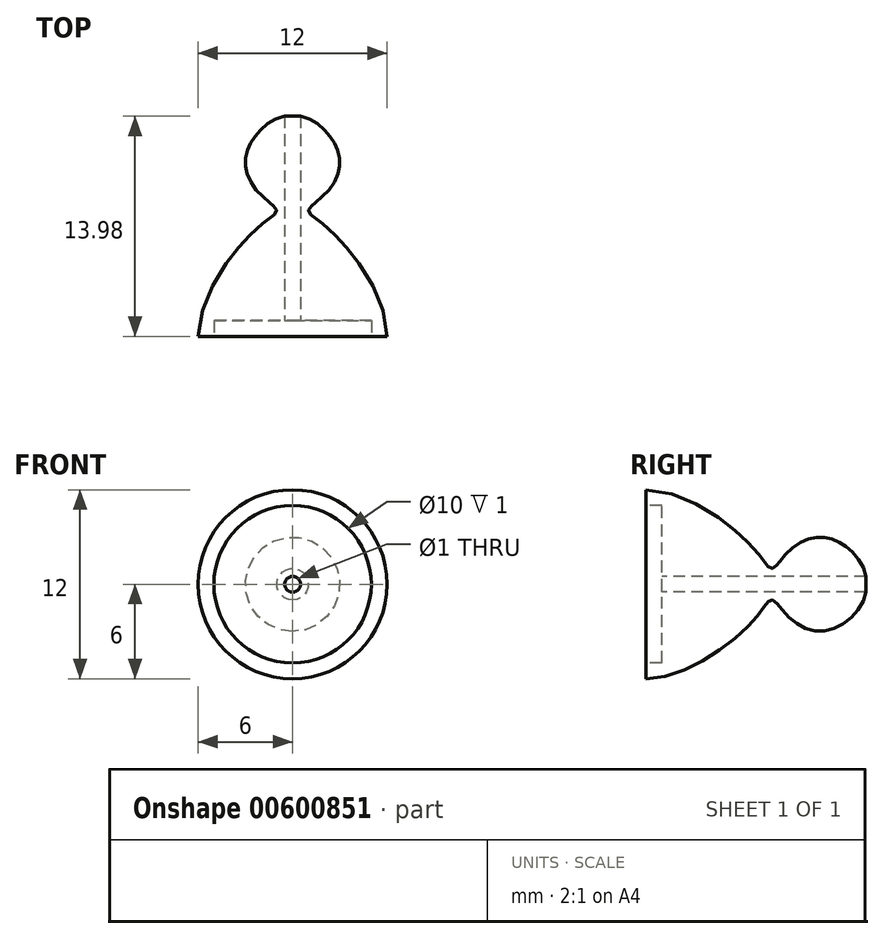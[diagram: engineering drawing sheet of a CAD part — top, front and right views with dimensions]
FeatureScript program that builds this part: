
annotation { "Feature Type Name" : "Feature", "Feature Type Description" : "" }
export const myFeature = defineFeature(function(context is Context, id is Id, definition is map)
    precondition{}
    {
        {
            var Q0;
            Q0=qCreatedBy(makeId("Right.planeOp"),FACE);
            var sketch = newSketch(context, id + "F0", { "sketchPlane" : qUnion([Q0])});
            skFitSpline(sketch, "E0", {"points": [v(0, -6) * mm, v(7.09, -2) * mm, v(8, -1) * mm, v(8.97, -2) * mm, v(11, -3) * mm, v(13.15, -2) * mm, v(14, 0) * mm], "startDerivative": vector(28.8, 0.35) * mm, "endDerivative": vector(-1.38, 13.65) * mm});
            skLineSegment(sketch, "E1", {"start": v(0, 0) * mm, "end": v(14, 0) * mm});
            skLineSegment(sketch, "E2", {"start": v(0, -6) * mm, "end": v(0, 0) * mm});
            skSolve(sketch);
        }
        {
            var Q0;
            Q0=makeQuery(id+"F0.imprint","IMPRINT",FACE,{"disambiguationData":[TD([[makeQuery(id+"F0.imprint","IMPRINT",EDGE,{"derivedFrom":sQuery(id+"F0.wireOp",EDGE,"E0")}),1.0]])]});
            var Q1;
            Q1=sQuery(id+"F0.wireOp",EDGE,"E0");
            var Q2;
            Q2=sQuery(id+"F0.wireOp",EDGE,"E2");
            var Q3;
            Q3=sQuery(id+"F0.wireOp",EDGE,"E1");
            revolve(context, id + "F1", {"entities" : qUnion([Q0]), "surfaceEntities" : qUnion([Q1, Q2]), "axis" : qUnion([Q3]), "revolveType" : RevolveType.FULL});
        }
        {
            var Q0;
            Q0=qCreatedBy(makeId("Front.planeOp"),FACE);
            var sketch = newSketch(context, id + "F2", { "sketchPlane" : qUnion([Q0])});
            skCircle(sketch, "E3", {"center": v(0, 0) * mm, "radius": 5 * mm});
            skSolve(sketch);
        }
        {
            var Q0;
            Q0 = qSketchRegion(id + "F2", true);
            extrude(context, id + "F3", {"entities" : qUnion([Q0]), "operationType" : NewBodyOperationType.REMOVE, "oppositeDirection" : true, "depth" : 1 * mm, "offsetDistance" : 25 * mm});
        }
        {
            var Q0;
            Q0=qCreatedBy(makeId("Front.planeOp"),FACE);
            var sketch = newSketch(context, id + "F4", { "sketchPlane" : qUnion([Q0])});
            skCircle(sketch, "E4", {"center": v(0, 0) * mm, "radius": 0.5 * mm});
            skSolve(sketch);
        }
        {
            var Q0;
            Q0 = qSketchRegion(id + "F4", true);
            extrude(context, id + "F5", {"entities" : qUnion([Q0]), "operationType" : NewBodyOperationType.REMOVE, "oppositeDirection" : true, "depth" : 25 * mm, "offsetDistance" : 25 * mm});
        }
    });
